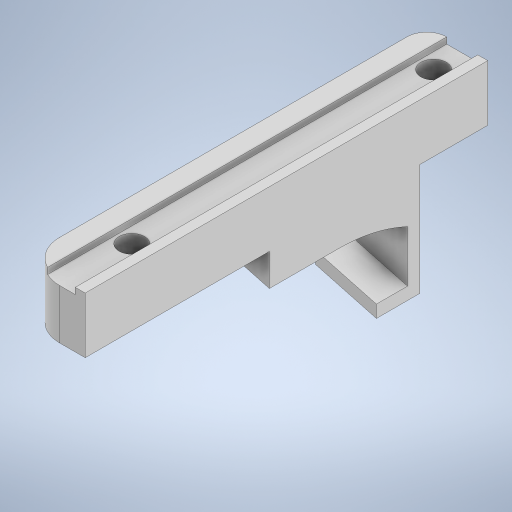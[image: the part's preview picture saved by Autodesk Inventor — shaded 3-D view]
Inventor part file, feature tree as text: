
AUTODESK INVENTOR PART (.ipt)
format: ipt  version: 2024 (Build 280153000, 153)  size: 316,928 bytes
history: native  units: in
note: dims shown in document units (in); Inventor stores cm internally (conversion verified against a paired STEP export)
features: extrude x7, sketch x4, plane x2
ambient origin geometry x8: Origin, YZ Plane, XZ Plane, XY Plane, X Axis, Y Axis, Z Axis, Center Point
bodies: Solid1 (feature_tree)
feature tree (13):
  sketch  "Sketch1"  dims[d1=2.3622in d3=0.3937in d4=0.126in d5=0.1614in d6=0.3819in d7=0.2559in d8=0.3937in d9=0.1181in d10=0.0354in d11=0.126in d12=0.2874in d13=0.3937in d14=0.2362in d15=0.0in]
  extrude  "Extrusion1"  Depth=0.2362in TaperAngle=0.0deg
  extrude  "Extrusion2"  Depth=0.1181in TaperAngle=0.0deg
  extrude  "Extrusion3"  Depth=0.0787in TaperAngle=0.0deg
  sketch  "Sketch2"  dims[d16=0.1969in d17=0.0in d18=0.1181in d19=0.0in]
  plane  "Work Plane1"
  sketch  "Sketch3"  dims[d20=0.874in d25=0.0787in d26=0.0in]
  extrude  "Extrusion4"  Depth=0.1969in TaperAngle=0.0deg
  extrude  "Extrusion5"  Depth=0.0787in
  extrude  "Extrusion6"  TaperAngle=15.0deg  [1 undecoded]
  plane  "Work Plane3"
  extrude  "Extrusion7"  Depth=0.315in
  sketch  "Sketch5"  dims[d27=0.874in d28=0.0in d29=0.1969in d30=0.0in d32=0.0945in d34=15.0deg d35=0.315in d36=0.0787in d37=0.0945in d38=0.0in d39=0.0in]
note: 1 required parameter value undecoded (feature->parameter linkage not recoverable at this tier; creation-order binding heuristic only, values carry confidence <= 0.55)
